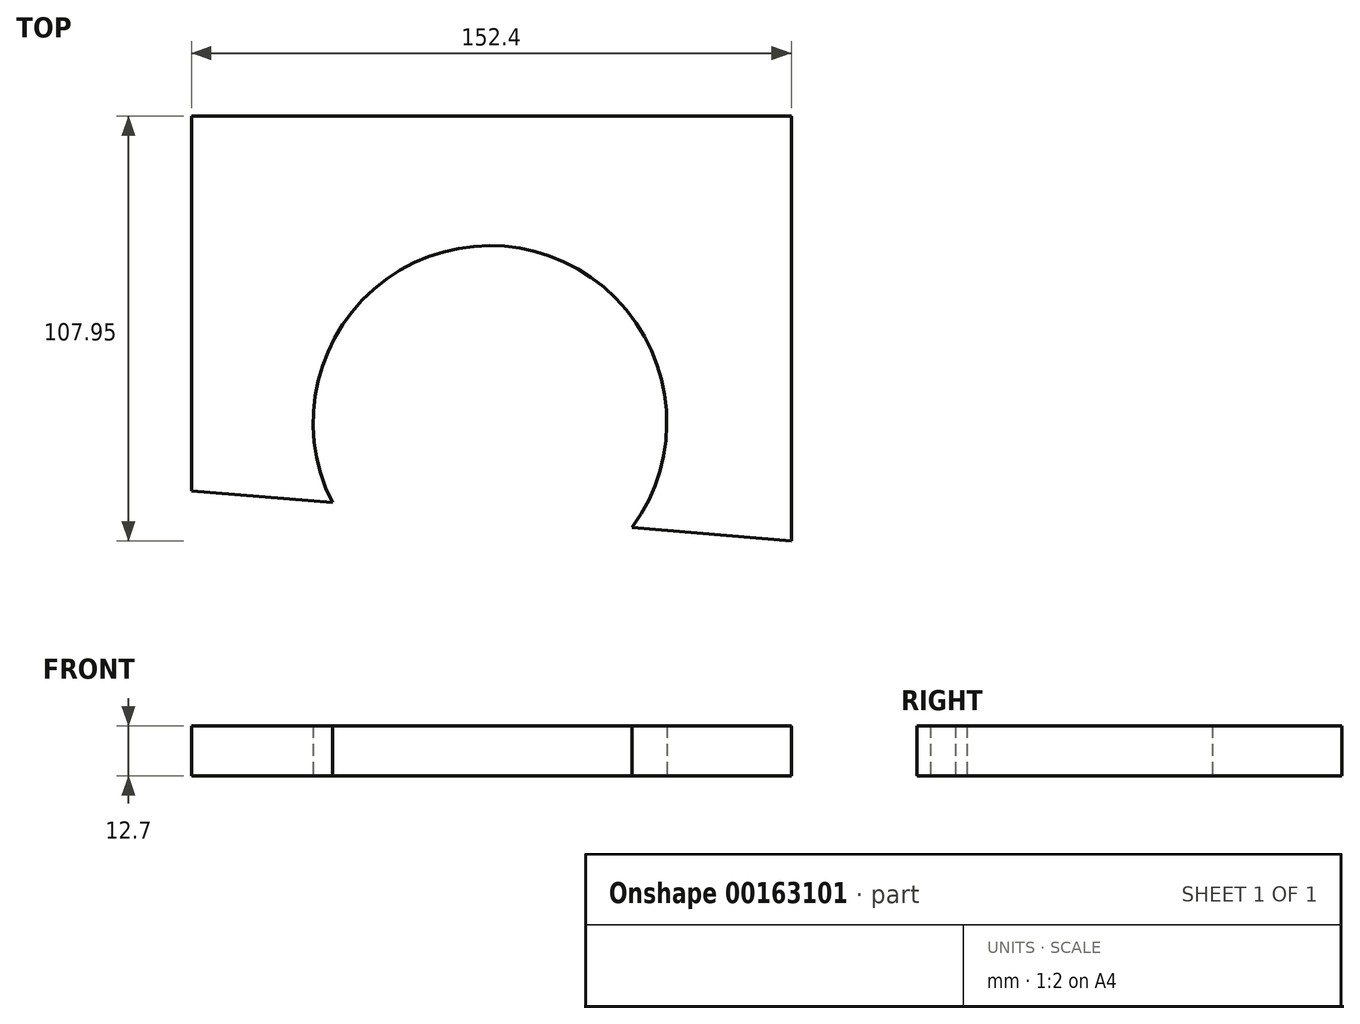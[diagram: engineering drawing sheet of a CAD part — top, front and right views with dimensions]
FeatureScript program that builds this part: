
annotation { "Feature Type Name" : "Feature", "Feature Type Description" : "" }
export const myFeature = defineFeature(function(context is Context, id is Id, definition is map)
    precondition{}
    {
        {
            var Q0;
            Q0=qCreatedBy(makeId("Top.planeOp"),FACE);
            var sketch = newSketch(context, id + "F0", { "sketchPlane" : qUnion([Q0])});
            skLineSegment(sketch, "E0", {"start": v(-75.87, 58.97) * mm, "end": v(-75.87, -36.28) * mm});
            skLineSegment(sketch, "E1", {"start": v(-75.87, 58.97) * mm, "end": v(76.53, 58.97) * mm});
            skLineSegment(sketch, "E2", {"start": v(76.53, 58.97) * mm, "end": v(76.53, -48.98) * mm});
            skCircle(sketch, "E3", {"center": v(0, -18.89) * mm, "radius": 44.91 * mm});
            skLineSegment(sketch, "E4", {"start": v(-75.87, -36.28) * mm, "end": v(76.53, -48.98) * mm});
            skSolve(sketch);
        }
        {
            var Q0;
            {var subQ5=sQuery(id+"F0.wireOp",EDGE,"E0");Q0=makeQuery(id+"F0.imprint","IMPRINT",FACE,{"disambiguationData":[TD([[makeQuery(id+"F0.imprint","IMPRINT",EDGE,{"derivedFrom":subQ5}),1.0]])]});}
            extrude(context, id + "F1", {"entities" : qUnion([Q0]), "depth" : 12.7 * mm});
        }
    });
